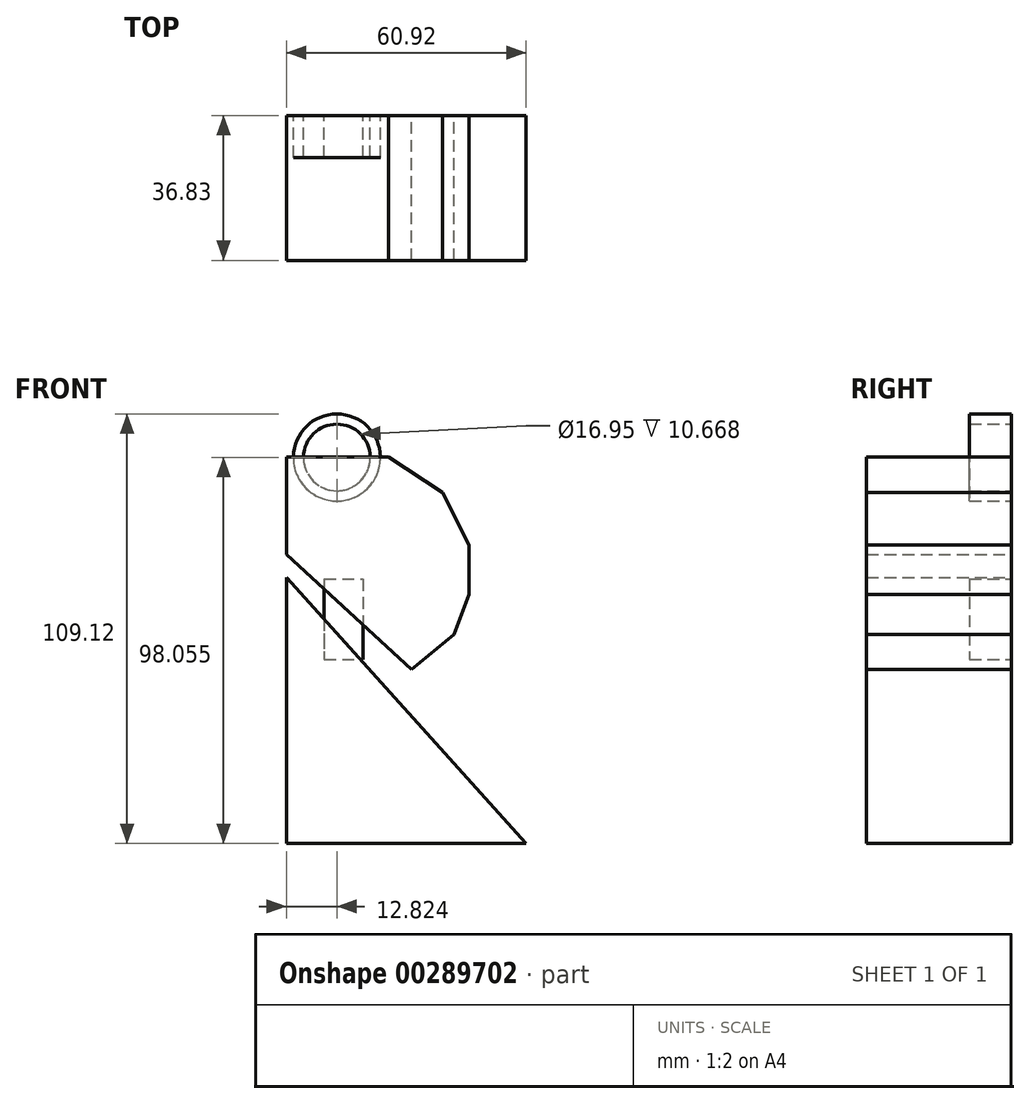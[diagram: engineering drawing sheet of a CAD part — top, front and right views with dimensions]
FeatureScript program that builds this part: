
annotation { "Feature Type Name" : "Feature", "Feature Type Description" : "" }
export const myFeature = defineFeature(function(context is Context, id is Id, definition is map)
    precondition{}
    {
        {
            var Q0;
            Q0=qCreatedBy(makeId("Front.planeOp"),FACE);
            var sketch = newSketch(context, id + "F0", { "sketchPlane" : qUnion([Q0])});
            skLineSegment(sketch, "E0", {"start": v(-25.94, 23.46) * mm, "end": v(34.98, -44.16) * mm});
            skLineSegment(sketch, "E1", {"start": v(34.98, -44.16) * mm, "end": v(-25.94, -44.16) * mm});
            skLineSegment(sketch, "E2", {"start": v(-25.94, -44.16) * mm, "end": v(-25.94, 23.46) * mm});
            skLineSegment(sketch, "E3", {"start": v(-25.94, 29.3) * mm, "end": v(-25.94, 54.07) * mm});
            skLineSegment(sketch, "E4", {"start": v(-25.94, 54.07) * mm, "end": v(0, 54.07) * mm});
            skLineSegment(sketch, "E5", {"start": v(0, 54.07) * mm, "end": v(13.7, 45.03) * mm});
            skLineSegment(sketch, "E6", {"start": v(13.7, 45.03) * mm, "end": v(20.4, 31.63) * mm});
            skLineSegment(sketch, "E7", {"start": v(20.4, 31.63) * mm, "end": v(20.4, 19.1) * mm});
            skLineSegment(sketch, "E8", {"start": v(20.4, 19.1) * mm, "end": v(16.61, 8.9) * mm});
            skLineSegment(sketch, "E9", {"start": v(16.61, 8.9) * mm, "end": v(5.83, 0) * mm});
            skLineSegment(sketch, "E10", {"start": v(5.83, 0) * mm, "end": v(-25.94, 29.3) * mm});
            skSolve(sketch);
        }
        {
            var Q0;
            Q0 = qSketchRegion(id + "F0", true);
            extrude(context, id + "F1", {"entities" : qUnion([Q0]), "depth" : 36.83 * mm});
        }
        {
            var Q0;
            Q0=qCreatedBy(makeId("Front.planeOp"),FACE);
            var sketch = newSketch(context, id + "F2", { "sketchPlane" : qUnion([Q0])});
            skLineSegment(sketch, "E11.bottom", {"start": v(-16.32, 23) * mm, "end": v(-6.41, 23) * mm});
            skLineSegment(sketch, "E11.top", {"start": v(-16.32, 2.6) * mm, "end": v(-6.41, 2.6) * mm});
            skLineSegment(sketch, "E11.left", {"start": v(-16.32, 23) * mm, "end": v(-16.32, 2.6) * mm});
            skLineSegment(sketch, "E11.right", {"start": v(-6.41, 23) * mm, "end": v(-6.41, 2.6) * mm});
            skCircle(sketch, "E12", {"center": v(-13.12, 53.9) * mm, "radius": 11.06 * mm});
            skCircle(sketch, "E13", {"center": v(-13.12, 53.9) * mm, "radius": 8.47 * mm});
            skSolve(sketch);
        }
        {
            var Q0;
            Q0 = qSketchRegion(id + "F2", true);
            extrude(context, id + "F3", {"entities" : qUnion([Q0]), "depth" : 10.67 * mm});
        }
    });
